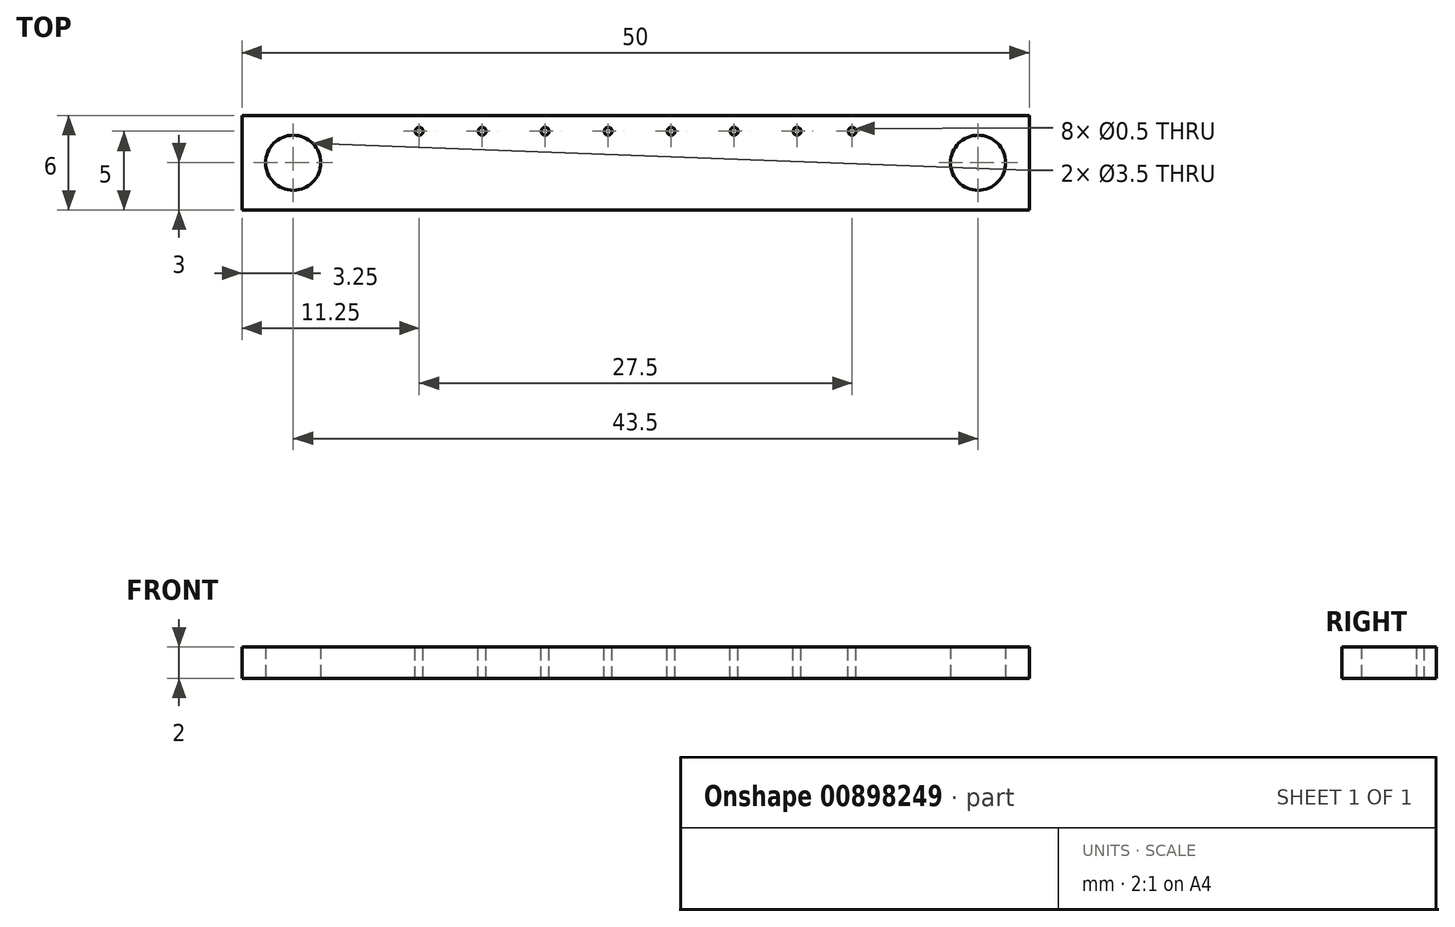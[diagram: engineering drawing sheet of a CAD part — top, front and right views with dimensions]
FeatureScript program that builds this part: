
annotation { "Feature Type Name" : "Feature", "Feature Type Description" : "" }
export const myFeature = defineFeature(function(context is Context, id is Id, definition is map)
    precondition{}
    {
        {
            var Q0;
            Q0=qCreatedBy(makeId("Top.planeOp"),FACE);
            var sketch = newSketch(context, id + "F0", { "sketchPlane" : qUnion([Q0])});
            skLineSegment(sketch, "E0.bottom", {"start": v(0, 0) * mm, "end": v(50, 0) * mm});
            skLineSegment(sketch, "E0.top", {"start": v(0, 6) * mm, "end": v(50, 6) * mm});
            skLineSegment(sketch, "E0.left", {"start": v(0, 0) * mm, "end": v(0, 6) * mm});
            skLineSegment(sketch, "E0.right", {"start": v(50, 0) * mm, "end": v(50, 6) * mm});
            skCircle(sketch, "E1", {"center": v(3.25, 3) * mm, "radius": 1.75 * mm});
            skCircle(sketch, "E2", {"center": v(46.75, 3) * mm, "radius": 1.75 * mm});
            skSolve(sketch);
        }
        {
            var Q0;
            Q0=qSketchRegion(id+"F0",true);
            extrude(context, id + "F1", {"entities" : qUnion([Q0]), "depth" : 2 * mm, "offsetDistance" : 25 * mm});
        }
        {
            var Q0;
            Q0=makeQuery(id+"F1.opExtrude","CAP_FACE",FACE,{"disambiguationData":[OSD([sQuery(id+"F0.wireOp",EDGE,"E0.bottom"),sQuery(id+"F0.wireOp",EDGE,"E0.top"),sQuery(id+"F0.wireOp",EDGE,"E0.left"),sQuery(id+"F0.wireOp",EDGE,"E0.right"),sQuery(id+"F0.wireOp",EDGE,"E1"),sQuery(id+"F0.wireOp",EDGE,"E2")])],"isStart":false});
            var sketch = newSketch(context, id + "F2", { "sketchPlane" : qUnion([Q0])});
            skCircle(sketch, "E3", {"center": v(11.25, 5) * mm, "radius": 0.25 * mm});
            skCircle(sketch, "E4.1.0.0", {"center": v(15.25, 5) * mm, "radius": 0.25 * mm});
            skCircle(sketch, "E4.2.0.0", {"center": v(19.25, 5) * mm, "radius": 0.25 * mm});
            skCircle(sketch, "E4.3.0.0", {"center": v(23.25, 5) * mm, "radius": 0.25 * mm});
            skCircle(sketch, "E4.4.0.0", {"center": v(27.25, 5) * mm, "radius": 0.25 * mm});
            skCircle(sketch, "E4.5.0.0", {"center": v(31.25, 5) * mm, "radius": 0.25 * mm});
            skCircle(sketch, "E4.6.0.0", {"center": v(35.25, 5) * mm, "radius": 0.25 * mm});
            skLineSegment(sketch, "E4.direction1", {"start": v(11.25, 5) * mm, "end": v(15.25, 5) * mm, "construction": true});
            skCircle(sketch, "E5", {"center": v(38.75, 5) * mm, "radius": 0.25 * mm});
            skSolve(sketch);
        }
        {
            var Q0;
            Q0 = qSketchRegion(id + "F2", true);
            extrude(context, id + "F3", {"entities" : qUnion([Q0]), "operationType" : NewBodyOperationType.REMOVE, "endBound" : BoundingType.THROUGH_ALL, "oppositeDirection" : true, "depth" : 25 * mm, "offsetDistance" : 25 * mm});
        }
    });
